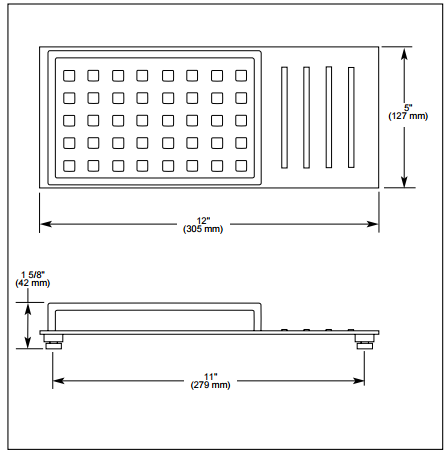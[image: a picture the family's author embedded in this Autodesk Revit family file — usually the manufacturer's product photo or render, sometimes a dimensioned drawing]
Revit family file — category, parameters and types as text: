
# Revit family: Tray-Delta-Vero-Vanity
name_source: partatom
category: Furniture
revit_build: Autodesk Revit MEP 2012 (Build: 20110916_2132(x64)
units: mm (PartAtom-declared; Revit-internal decimal feet)

## types (4) — shared parameters
Date Modified = July 17, 2015
Default Elevation = 48 "
Depth = 5 "
Equipment Abbreviation = VT
Family Version = 1.0
Height = 1.625 "
Manufacturer = Delta Faucet Company
Model Disclaimer = Contact Delta Faucet Company for More Information
Product Documentation Link = http://www.deltafaucet.com
Product Page URL = http://www.deltafaucet.com
URL = http://www.deltafaucet.com
Width = 12 "
z Bar Width = 4.75 "
z Height = 1.625 "
z Length = 12 "
z Width = 5 "
zero-valued in all types: z Elevation

## per-type parameters (varying)
| type | Description | Model | Product Material | z Type |
| Chrome | Vero Vanity Tray, Chrome | 77612 | Chrome - Delta - Polished | 1 |
| Champagne Bronze | Vero Vanity Tray, Champagne Bronze | 77612-CZ | Bronze - Delta - Champagne | 2 |
| Venetian Bronze | Vero Vanity Tray, Venetian Bronze | 77612-RB | Bronze - Delta - Venetian | 3 |
| Stainless | Vero Vanity Tray, Stainless | 77612-SS | Stainless Steel - Delta - Polished | 4 |

## geometry (parser evidence)
native form markers: Blend x14, Sweep x2
no freeform markers — native parametric forms only
